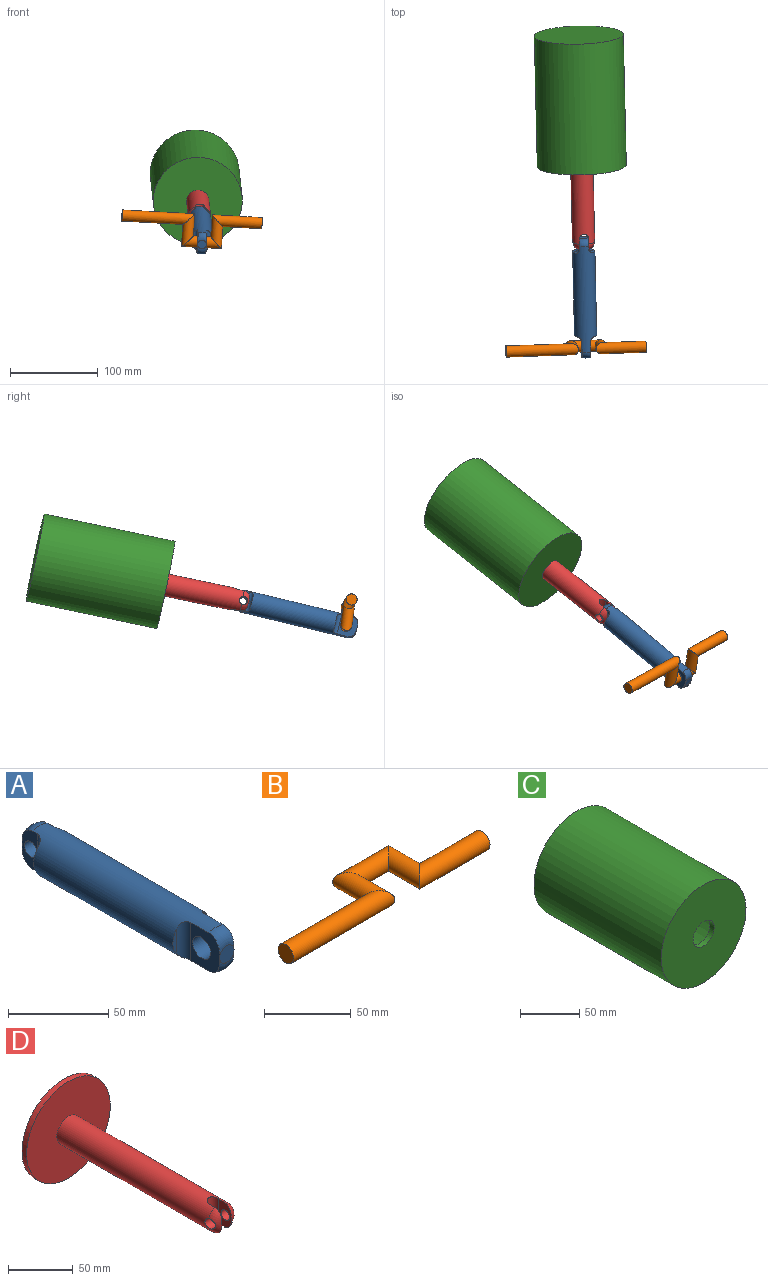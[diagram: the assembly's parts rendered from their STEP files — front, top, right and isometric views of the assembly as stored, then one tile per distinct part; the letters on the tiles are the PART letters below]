
ASSEMBLY  parts=4 mates=3
PART A: 25 faces, bbox 25.4x139.7x25.4 mm
  f0: plane 15.24x2.54mm, normal (0,-1,0), area 26.4mm2, adj f1,f17
  f1: cylinder r=12.7mm len=124.46mm, axis (0,1,0), area 8449.5mm2, adj f0,f2,f3,f4,f7,f8,f9,f10
  f2: plane 15.24x2.54mm, normal (0,-1,0), area 26.4mm2, adj f1,f18
  f3: plane 23.28x10.8mm, normal (-1,0,0), area 157.3mm2, adj f1,f6,f7,f8,f19,f21
  f4: plane 23.28x10.8mm, normal (1,0,0), area 157.3mm2, adj f1,f6,f7,f8,f22,f24
  f5: plane 10.16x10.16mm, normal (0,1,0), area 81.1mm2, adj f7,f8
  f6: cylinder r=4.57mm len=10.16mm, axis (-1,0,0), area 291.9mm2, adj f3,f4,f20,f23
  f7: torus R=5.08mm, axis (0,-1,0), area 130.8mm2, adj f1,f3,f4,f5
  f8: torus R=5.08mm, axis (0,-1,0), area 130.8mm2, adj f1,f3,f4,f5
  f9: plane 15.24x2.54mm, normal (0,1,0), area 26.4mm2, adj f1,f19,f20,f21
  f10: plane 15.24x2.54mm, normal (0,1,0), area 26.4mm2, adj f1,f22,f23,f24
  f11: plane 23.28x20.32mm, normal (-1,0,0), area 317.8mm2, adj f1,f14,f15,f16,f17
  f12: plane 23.28x20.32mm, normal (1,0,0), area 317.8mm2, adj f1,f14,f15,f16,f18
  f13: plane 10.16x10.16mm, normal (0,-1,0), area 81.1mm2, adj f14,f15
  f14: torus R=5.08mm, axis (0,-1,0), area 130.8mm2, adj f1,f11,f12,f13
  f15: torus R=5.08mm, axis (0,-1,0), area 130.8mm2, adj f1,f11,f12,f13
  f16: cylinder r=6.35mm len=12.7mm, axis (-1,0,0), area 405.4mm2, adj f11,f12
  f17: cylinder r=5.08mm len=23.28mm, axis (0,0,-1), area 167mm2, adj f0,f1,f11
  f18: cylinder r=5.08mm len=23.28mm, axis (0,0,1), area 167mm2, adj f1,f2,f12
  f19: cylinder r=5.08mm len=10.57mm, axis (0,0,1), area 75mm2, adj f1,f3,f9,f20
  f20: bspline ~5.24x5.23mm, area 16.9mm2, adj f6,f9,f19,f21
  f21: cylinder r=5.08mm len=10.57mm, axis (0,0,1), area 75mm2, adj f1,f3,f9,f20
  f22: cylinder r=5.08mm len=10.57mm, axis (0,0,-1), area 75mm2, adj f1,f4,f10,f23
  f23: bspline ~5.29x5.27mm, area 16.9mm2, adj f6,f10,f22,f24
  f24: cylinder r=5.08mm len=10.57mm, axis (0,0,-1), area 75mm2, adj f1,f4,f10,f23
PART B: 7 faces, bbox 160x38.1x12.7 mm
  f0: plane 12.7x12.7mm, normal (1,0,0), area 126.7mm2, adj f2
  f1: plane 12.7x12.7mm, normal (-1,0,0), area 126.7mm2, adj f6
  f2: cylinder r=6.35mm len=57.15mm, axis (1,0,0), area 2026.8mm2, adj f0,f3
  f3: cylinder r=6.35mm len=38.1mm, axis (0,-1,0), area 1013.4mm2, adj f2,f4
  f4: cylinder r=6.35mm len=45.72mm, axis (1,0,0), area 1317.4mm2, adj f3,f5
  f5: cylinder r=6.35mm len=38.1mm, axis (0,1,0), area 1004.8mm2, adj f4,f6
  f6: cylinder r=6.35mm len=82.55mm, axis (1,0,0), area 3031.6mm2, adj f1,f5
PART C: 7 faces, bbox 101.6x152.4x101.6 mm
  f0: plane 91.44x91.44mm, normal (0,-1,0), area 6566.9mm2, adj f1
  f1: cylinder r=45.72mm len=142.24mm, axis (0,-1,0), area 40860.9mm2, adj f0,f4
  f2: cylinder r=50.8mm len=152.4mm, axis (0,-1,0), area 48643.9mm2, adj f3,f6
  f3: plane 101.6x101.6mm, normal (0,-1,0), area 7600.6mm2, adj f2,f5
  f4: plane 91.44x91.44mm, normal (0,1,0), area 6060.2mm2, adj f1,f5
  f5: cylinder r=12.7mm len=25.4mm, axis (0,-1,0), area 405.4mm2, adj f3,f4
  f6: plane 101.6x101.6mm, normal (0,1,0), area 8107.3mm2, adj f2
PART D: 11 faces, bbox 91.4x177.8x91.4 mm
  f0: cylinder r=12.7mm len=165.1mm, axis (0,1,0), area 12915.5mm2, adj f2,f4,f5,f6,f7,f8,f9,f10
  f1: cylinder r=45.72mm len=91.44mm, axis (0,1,0), area 1459.3mm2, adj f2,f3
  f2: plane 91.44x91.44mm, normal (0,-1,0), area 6060.2mm2, adj f0,f1
  f3: plane 91.44x91.44mm, normal (0,1,0), area 6566.9mm2, adj f1
  f4: plane 23.28x13.97mm, normal (1,0,0), area 231mm2, adj f0,f7,f8,f10
  f5: plane 23.28x13.97mm, normal (-1,0,0), area 231mm2, adj f0,f6,f9,f10
  f6: cylinder r=4.57mm len=9.14mm, axis (-1,0,0), area 185.1mm2, adj f0,f5,f9
  f7: cylinder r=4.57mm len=9.14mm, axis (-1,0,0), area 185.1mm2, adj f0,f4,f8
  f8: torus R=5.08mm, axis (0,-1,0), area 192.9mm2, adj f0,f4,f7
  f9: torus R=5.08mm, axis (0,-1,0), area 192.9mm2, adj f0,f5,f6
  f10: cylinder r=5.08mm len=25.4mm, axis (0,0,1), area 388.4mm2, adj f0,f4,f5
PLACE A rot(axis=(0.96,0.24,0.11),14deg) t=(-768.69,72.35,16.86)mm
PLACE B rot(axis=(-1,0.01,0.05),82.7deg) t=(-776.73,-255.35,-35.16)mm
PLACE C rot(axis=(0.95,0.27,0.13),12.4deg) t=(-769.76,103.03,16.83)mm
PLACE D rot(axis=(0.01,-0.99,-0.1),176.7deg) t=(-768.15,33.47,2.24)mm
MATE revolute A.f6 <-> D.f6  axis (-1,-0.03,0.05) through (-769.33,-134.47,-32.67)mm
MATE revolute B.f4 <-> A.f16  axis (1,0.03,-0.05) through (-761.75,-251.56,-61.21)mm
MATE slider D.f1 <-> C.f2  axis (0.02,-0.98,-0.21) through (-768.15,33.47,2.24)mm
